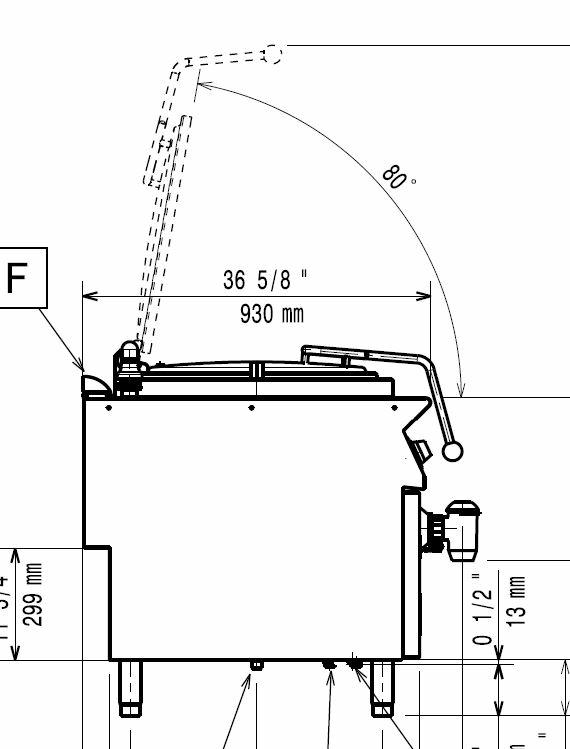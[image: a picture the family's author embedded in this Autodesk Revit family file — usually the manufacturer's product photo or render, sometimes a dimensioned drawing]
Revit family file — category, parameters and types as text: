
# Revit family: QF_ELECTROLUXPROFESSIONAL_391609_E9NNDTBAMEI
name_source: partatom
category: Attrezzature speciali
units: mm (PartAtom-declared; Revit-internal decimal feet)

## family parameters
Basato su piano di lavoro = No
Condiviso = No
Punto di calcolo locali = No
Quota connettore circolare = Usa diametro
Sempre verticale = Sì
Taglio con vuoti quando caricato = No
Tipo di parte = Normale

## types (1)
- Standard
    Accessory = Sì
    Cold Water Size = 1"
    Compressed Air Pressure = 0.00 psi
    Compressed Air Size = 0"
    Compressed Air Volume = 0 GPM
    Condensate Return Size = 0"
    Cycle = 60 Hz
    Depth Actual = 930 mm  [stored 3.05118 ft]
    Descrizione = 100LT GAS BOILING PAN-DIRECT HEATING-60HZ - QMARK
    Direct Waste Size = 2"
    Gas Input Pressure = 0.7
    Gas KW = 21
    Gas Size = 1"
    HP = 0.1 HP
    Height Actual = 850 mm  [stored 2.78871 ft]
    Hot Water Size = 1"
    Item Number = 391609
    Length Actual = 800 mm  [stored 2.62467 ft]
    Modello = E9NNDTBAMEI
    Phase = 1
    Produttore = Electrolux Professional
    Prospetto di default = 0 mm  [stored 0 ft]
    Refrigerant Compressor Remote = Sì
    Refrigeration Liquid Line Size = 0 mm  [stored 0 ft]
    Refrigeration Suction Line Size = 0 mm  [stored 0 ft]
    Steam Consumption per Hour = 0
    Steam Supply Maximum Pressure = 0.00 psi
    Steam Supply Minimum Pressure = 0.00 psi
    Steam Supply Size = 0"
    URL = https://www.electroluxprofessional.com
    URL Manufacturer = https://www.electroluxprofessional.com
    Volts = 220 V
    Watts = 100 W
    Weight = 135.00 kg

note: source unit labels omitted for Gas Input Pressure — the stored unit's dimension contradicts the parameter name (converter mislabeling)

note: [stored X ft] marks values corroborated as IEEE doubles in the binary element streams (Revit-internal decimal feet)

## geometry (parser evidence)
native form markers: Blend x9, Sweep x2
no freeform markers — native parametric forms only
